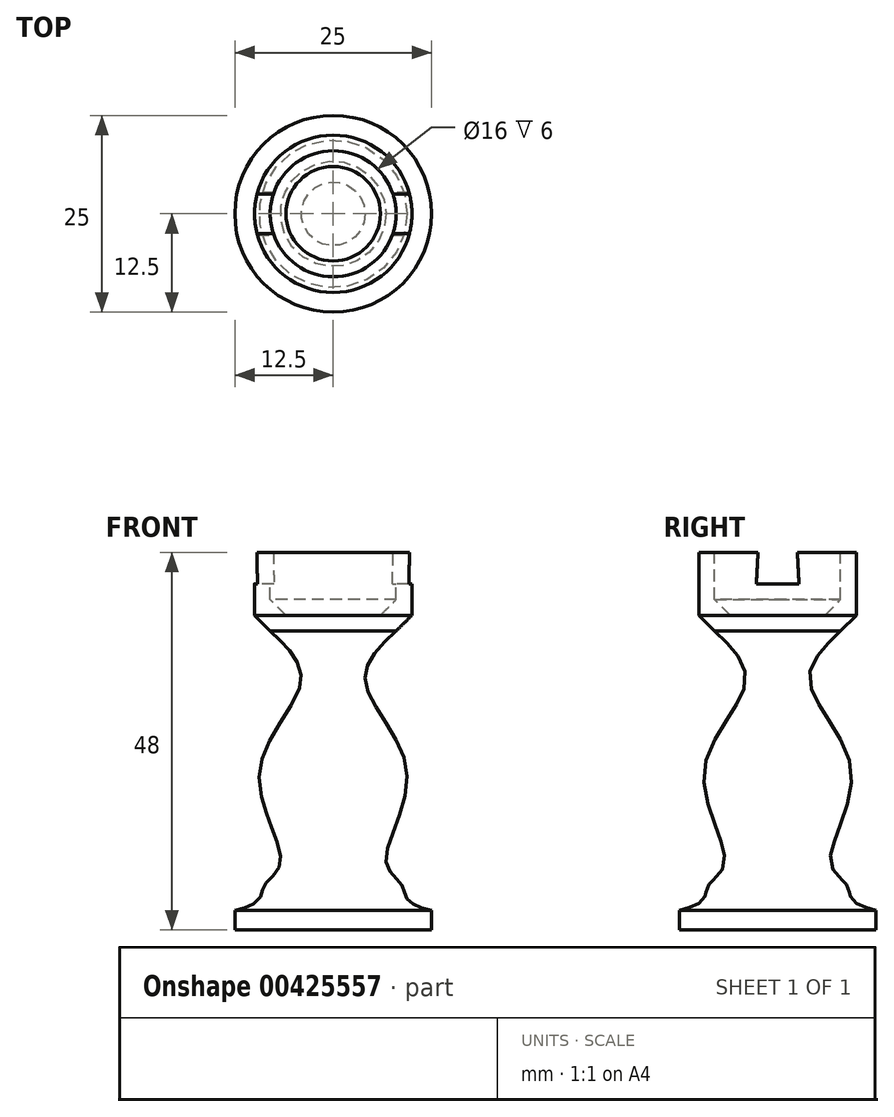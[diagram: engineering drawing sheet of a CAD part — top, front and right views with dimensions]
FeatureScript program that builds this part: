
annotation { "Feature Type Name" : "Feature", "Feature Type Description" : "" }
export const myFeature = defineFeature(function(context is Context, id is Id, definition is map)
    precondition{}
    {
        {
            var Q0;
            Q0=qCreatedBy(makeId("Front.planeOp"),FACE);
            var sketch = newSketch(context, id + "F0", { "sketchPlane" : qUnion([Q0])});
            skLineSegment(sketch, "E0.bottom", {"start": v(0, 0) * mm, "end": v(12.5, 0) * mm});
            skLineSegment(sketch, "E0.top", {"start": v(0, -48) * mm, "end": v(12.5, -48) * mm});
            skLineSegment(sketch, "E0.left", {"start": v(0, 0) * mm, "end": v(0, -48) * mm});
            skLineSegment(sketch, "E0.right", {"start": v(12.5, 0) * mm, "end": v(12.5, -48) * mm});
            skLineSegment(sketch, "E1.bottom", {"start": v(0, 0) * mm, "end": v(8, 0) * mm});
            skLineSegment(sketch, "E1.top", {"start": v(0, -8) * mm, "end": v(8, -8) * mm});
            skLineSegment(sketch, "E1.left", {"start": v(0, 0) * mm, "end": v(0, -8) * mm});
            skLineSegment(sketch, "E1.right", {"start": v(8, 0) * mm, "end": v(8, -8) * mm});
            skLineSegment(sketch, "E2.top", {"start": v(0, -45.5) * mm, "end": v(12.5, -45.5) * mm});
            skLineSegment(sketch, "E2.left", {"start": v(0, -48) * mm, "end": v(0, -45.5) * mm});
            skLineSegment(sketch, "E2.right", {"start": v(12.5, -48) * mm, "end": v(12.5, -45.5) * mm});
            skLineSegment(sketch, "E3", {"start": v(0, -10) * mm, "end": v(8, -10) * mm});
            skLineSegment(sketch, "E4", {"start": v(10, -8) * mm, "end": v(10, 0) * mm});
            skFitSpline(sketch, "E5", {"points": [v(8, -10) * mm, v(4.08, -16.39) * mm, v(9.37, -27.85) * mm, v(6.73, -39.4) * mm, v(8.76, -42.3) * mm, v(9.48, -44.19) * mm, v(12.5, -45.5) * mm], "startDerivative": vector(-34.1, -32.48) * mm, "endDerivative": vector(28.3, -7.6) * mm});
            skLineSegment(sketch, "E6", {"start": v(8, -10) * mm, "end": v(10, -8) * mm});
            skSolve(sketch);
        }
        {
            var Q0;
            {var subQ1=sQuery(id+"F0.wireOp",EDGE,"E1.top");Q0=makeQuery(id+"F0.imprint","IMPRINT",FACE,{"disambiguationData":[TD([[makeQuery(id+"F0.imprint","IMPRINT",EDGE,{"derivedFrom":subQ1}),-1.0]])]});}
            var Q1;
            {var subQ0=sQuery(id+"F0.wireOp",EDGE,"E2.top");Q1=makeQuery(id+"F0.imprint","IMPRINT",FACE,{"disambiguationData":[TD([[makeQuery(id+"F0.imprint","IMPRINT",EDGE,{"derivedFrom":subQ0}),1.0]])]});}
            var Q2;
            Q2=makeQuery(id+"F0.imprint","IMPRINT",FACE,{"disambiguationData":[TD([[makeQuery(id+"F0.imprint","IMPRINT",EDGE,{"derivedFrom":sQuery(id+"F0.wireOp",EDGE,"E0.top")}),1.0]])]});
            var Q3;
            Q3=sQuery(id+"F0.wireOp",EDGE,"E0.left");
            revolve(context, id + "F1", {"entities" : qUnion([Q0, Q1, Q2]), "axis" : qUnion([Q3]), "revolveType" : RevolveType.FULL});
        }
        {
            var Q0;
            Q0=makeQuery(id+"F1.opRevolve","SWEPT_FACE",FACE,{"disambiguationData":[OSD([sQuery(id+"F0.wireOp",EDGE,"E0.bottom")])]});
            var sketch = newSketch(context, id + "F2", { "sketchPlane" : qUnion([Q0])});
            skLineSegment(sketch, "E7.bottom", {"start": v(15, 2.5) * mm, "end": v(-15, 2.5) * mm});
            skLineSegment(sketch, "E7.top", {"start": v(15, -2.5) * mm, "end": v(-15, -2.5) * mm});
            skLineSegment(sketch, "E7.left", {"start": v(15, 2.5) * mm, "end": v(15, -2.5) * mm});
            skLineSegment(sketch, "E7.right", {"start": v(-15, 2.5) * mm, "end": v(-15, -2.5) * mm});
            skPoint(sketch, "E7.middle", {"position": v(0, 0) * mm});
            skSolve(sketch);
        }
        {
            var Q0;
            Q0 = qSketchRegion(id + "F2", true);
            extrude(context, id + "F3", {"entities" : qUnion([Q0]), "operationType" : NewBodyOperationType.REMOVE, "oppositeDirection" : true, "depth" : 4 * mm, "hasDraft" : true, "draftAngle" : 3 * degree});
        }
        {
            var Q0;
            Q0=makeQuery(id+"F1.opRevolve","SWEPT_FACE",FACE,{"disambiguationData":[OSD([sQuery(id+"F0.wireOp",EDGE,"E1.top")])]});
            chamfer(context, id + "F4", {"entities" : qUnion([Q0]), "width" : 2 * mm, "tangentPropagation" : true});
        }
    });
